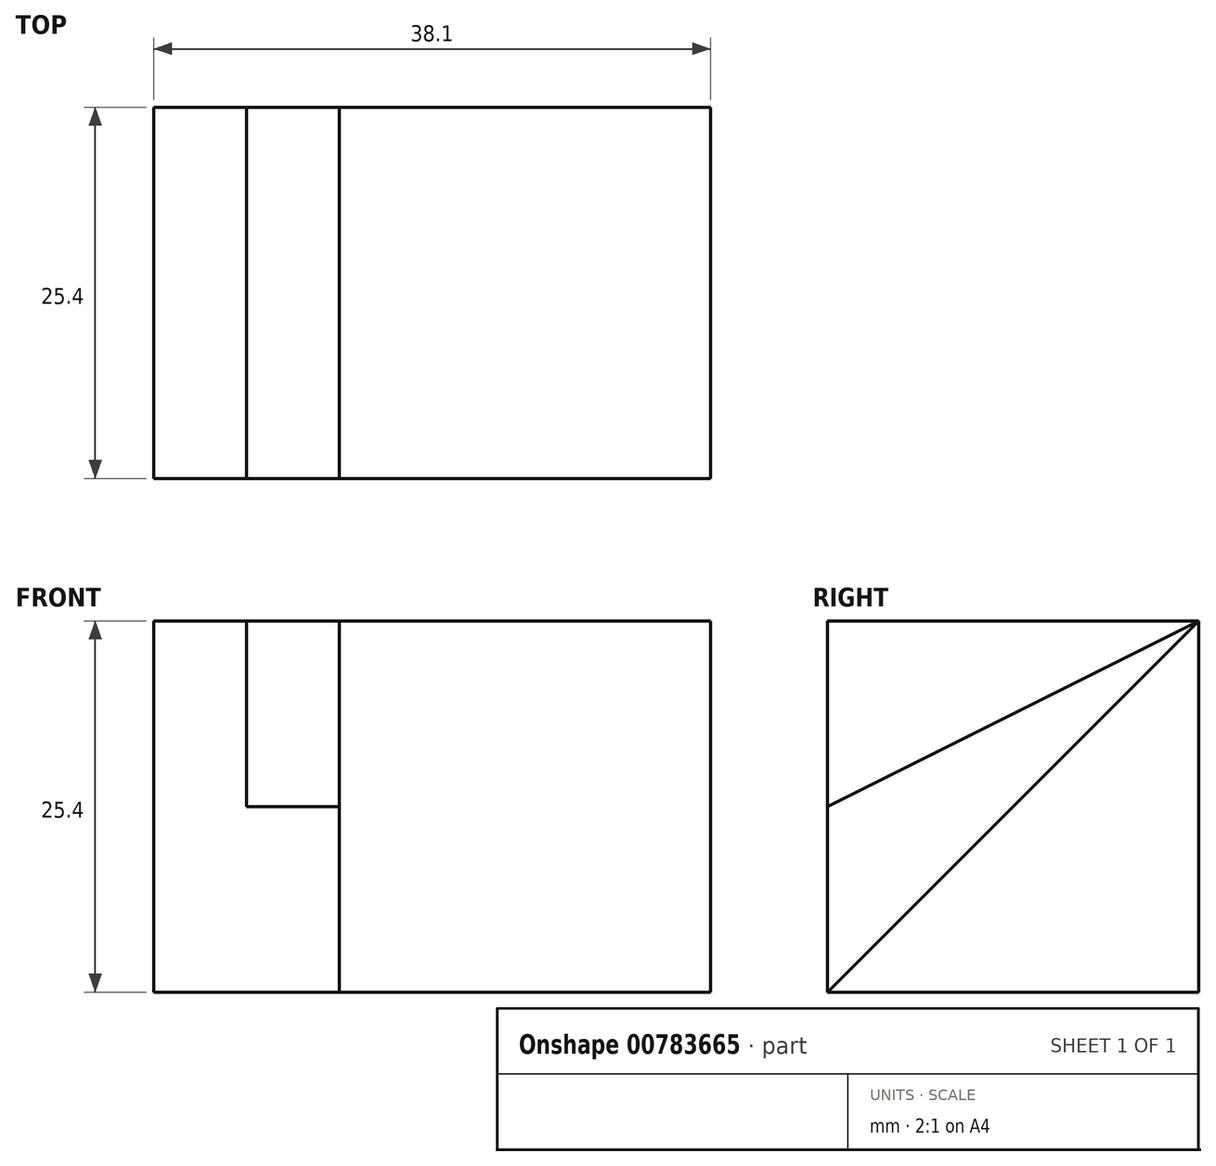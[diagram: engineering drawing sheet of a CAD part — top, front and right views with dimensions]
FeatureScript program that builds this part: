
annotation { "Feature Type Name" : "Feature", "Feature Type Description" : "" }
export const myFeature = defineFeature(function(context is Context, id is Id, definition is map)
    precondition{}
    {
        {
            var Q0;
            Q0=qCreatedBy(makeId("Front.planeOp"),FACE);
            var sketch = newSketch(context, id + "F0", { "sketchPlane" : qUnion([Q0])});
            skLineSegment(sketch, "E0", {"start": v(0, 0) * mm, "end": v(0, 25.4) * mm});
            skLineSegment(sketch, "E1", {"start": v(0, 25.4) * mm, "end": v(38.1, 25.4) * mm});
            skLineSegment(sketch, "E2", {"start": v(38.1, 25.4) * mm, "end": v(38.1, 0) * mm});
            skLineSegment(sketch, "E3", {"start": v(38.1, 0) * mm, "end": v(0, 0) * mm});
            skSolve(sketch);
        }
        {
            var Q0;
            Q0 = qSketchRegion(id + "F0", true);
            extrude(context, id + "F1", {"entities" : qUnion([Q0]), "depth" : 25.4 * mm, "offsetDistance" : 25.4 * mm});
        }
        {
            var Q0;
            Q0=makeQuery(id+"F1.opExtrude","SWEPT_FACE",FACE,{"disambiguationData":[OSD([sQuery(id+"F0.wireOp",EDGE,"E2")])]});
            var sketch = newSketch(context, id + "F2", { "sketchPlane" : qUnion([Q0])});
            skLineSegment(sketch, "E4", {"start": v(-25.4, 0) * mm, "end": v(0, 25.4) * mm});
            skSolve(sketch);
        }
        {
            var Q0;
            Q0=makeQuery(id+"F2.imprint","IMPRINT",FACE,{"disambiguationData":[TD([[makeQuery(id+"F2.imprint","IMPRINT",EDGE,{"derivedFrom":sQuery(id+"F2.wireOp",EDGE,"E4")}),1.0]])]});
            extrude(context, id + "F3", {"entities" : qUnion([Q0]), "operationType" : NewBodyOperationType.REMOVE, "oppositeDirection" : true, "depth" : 25.4 * mm, "offsetDistance" : 25.4 * mm});
        }
        {
            var Q0;
            Q0=makeQuery(id+"F3.boolean.opBoolean","COPY",FACE,{"derivedFrom":makeQuery(id+"F3.opExtrude","CAP_FACE",FACE,{"disambiguationData":[OSD([sQuery(id+"F0.wireOp",EDGE,"E1"),sQuery(id+"F0.wireOp",EDGE,"E2"),sQuery(id+"F2.wireOp",EDGE,"E4")])],"isStart":false})});
            var sketch = newSketch(context, id + "F4", { "sketchPlane" : qUnion([Q0])});
            skLineSegment(sketch, "E5", {"start": v(0, 25.4) * mm, "end": v(-25.4, 12.7) * mm});
            skSolve(sketch);
        }
        {
            var Q0;
            Q0 = qSketchRegion(id + "F4", true);
            var Q1;
            {var subQ0=sQuery(id+"F4.wireOp",EDGE,"E5");Q1=makeQuery(id+"F4.imprint","IMPRINT",FACE,{"disambiguationData":[TD([[makeQuery(id+"F4.imprint","IMPRINT",EDGE,{"derivedFrom":subQ0}),-1.0]])]});}
            extrude(context, id + "F5", {"entities" : qUnion([Q0, Q1]), "operationType" : NewBodyOperationType.REMOVE, "oppositeDirection" : true, "depth" : 6.35 * mm, "offsetDistance" : 25.4 * mm});
        }
    });
